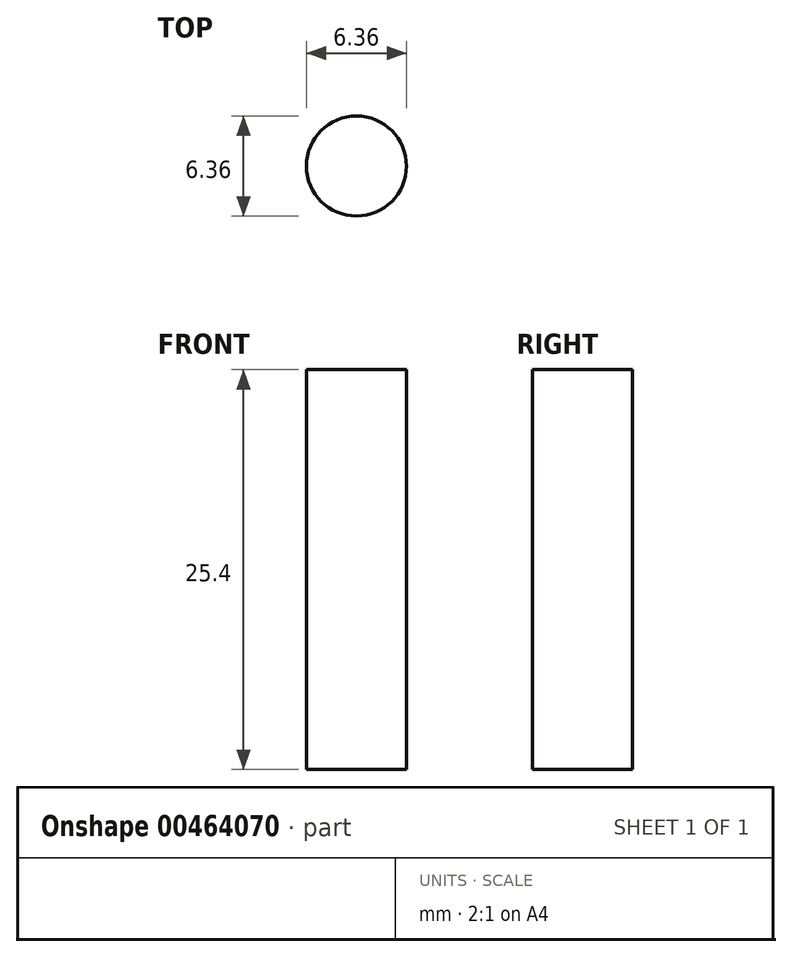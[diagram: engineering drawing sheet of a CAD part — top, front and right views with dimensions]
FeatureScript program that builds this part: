
annotation { "Feature Type Name" : "Feature", "Feature Type Description" : "" }
export const myFeature = defineFeature(function(context is Context, id is Id, definition is map)
    precondition{}
    {
        {
            var Q0;
            Q0=qCreatedBy(makeId("Top.planeOp"),FACE);
            var sketch = newSketch(context, id + "F0", { "sketchPlane" : qUnion([Q0])});
            skCircle(sketch, "E0", {"center": v(0, 0) * mm, "radius": 3.18 * mm});
            skSolve(sketch);
        }
        {
            var Q0;
            Q0 = qSketchRegion(id + "F0", true);
            extrude(context, id + "F1", {"entities" : qUnion([Q0]), "depth" : 25.4 * mm, "offsetDistance" : 25.4 * mm});
        }
    });
